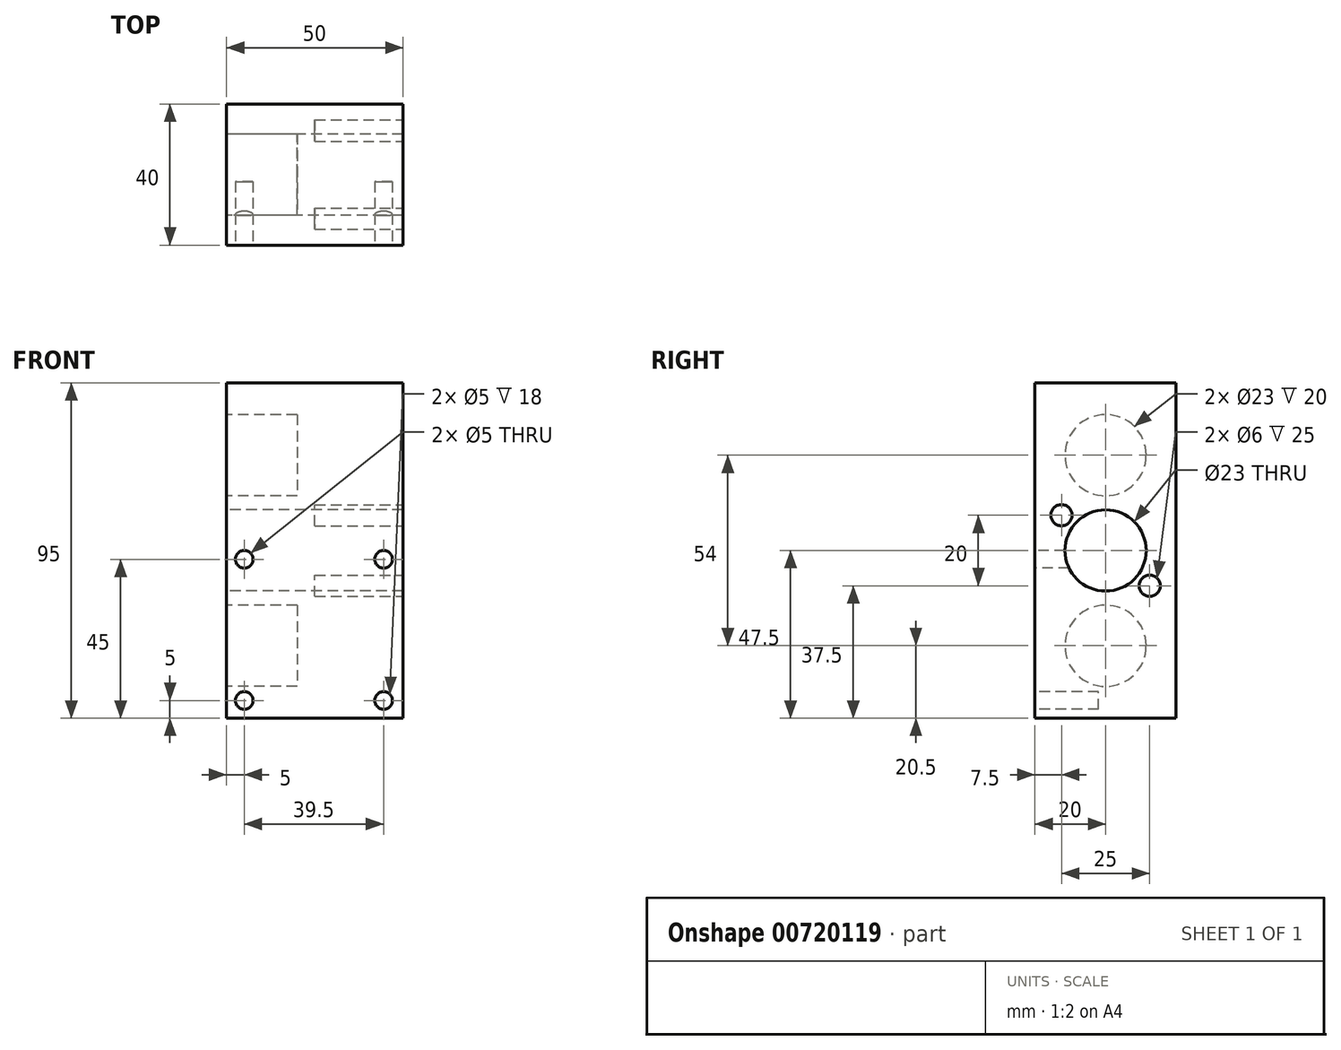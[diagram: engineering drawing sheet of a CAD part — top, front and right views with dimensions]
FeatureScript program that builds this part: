
annotation { "Feature Type Name" : "Feature", "Feature Type Description" : "" }
export const myFeature = defineFeature(function(context is Context, id is Id, definition is map)
    precondition{}
    {
        {
            var Q0;
            Q0=qCreatedBy(makeId("Front.planeOp"),FACE);
            var sketch = newSketch(context, id + "F0", { "sketchPlane" : qUnion([Q0])});
            skLineSegment(sketch, "E0.bottom", {"start": v(0, 0) * mm, "end": v(50, 0) * mm});
            skLineSegment(sketch, "E0.top", {"start": v(0, 95) * mm, "end": v(50, 95) * mm});
            skLineSegment(sketch, "E0.left", {"start": v(0, 0) * mm, "end": v(0, 95) * mm});
            skLineSegment(sketch, "E0.right", {"start": v(50, 0) * mm, "end": v(50, 95) * mm});
            skSolve(sketch);
        }
        {
            var Q0;
            Q0=makeQuery(id+"F0.imprint","IMPRINT",FACE,{"disambiguationData":[TD([[makeQuery(id+"F0.imprint","IMPRINT",EDGE,{"derivedFrom":sQuery(id+"F0.wireOp",EDGE,"E0.bottom")}),1.0]])]});
            extrude(context, id + "F1", {"entities" : qUnion([Q0]), "depth" : 40 * mm, "offsetDistance" : 25 * mm});
        }
        {
            var Q0;
            Q0=makeQuery(id+"F1.opExtrude","CAP_FACE",FACE,{"disambiguationData":[OSD([sQuery(id+"F0.wireOp",EDGE,"E0.bottom"),sQuery(id+"F0.wireOp",EDGE,"E0.top"),sQuery(id+"F0.wireOp",EDGE,"E0.left"),sQuery(id+"F0.wireOp",EDGE,"E0.right")])],"isStart":false});
            var sketch = newSketch(context, id + "F2", { "sketchPlane" : qUnion([Q0])});
            skCircle(sketch, "E1", {"center": v(5, 5) * mm, "radius": 2.5 * mm});
            skCircle(sketch, "E2", {"center": v(44.5, 5) * mm, "radius": 2.5 * mm});
            skCircle(sketch, "E3.0.1.0", {"center": v(5, 45) * mm, "radius": 2.5 * mm});
            skCircle(sketch, "E3.0.1.1", {"center": v(44.5, 45) * mm, "radius": 2.5 * mm});
            skLineSegment(sketch, "E3.direction1", {"start": v(5, 5) * mm, "end": v(30, 5) * mm, "construction": true});
            skLineSegment(sketch, "E3.direction2", {"start": v(5, 5) * mm, "end": v(5, 45) * mm, "construction": true});
            skSolve(sketch);
        }
        {
            var Q0;
            Q0 = qSketchRegion(id + "F2", true);
            extrude(context, id + "F3", {"entities" : qUnion([Q0]), "operationType" : NewBodyOperationType.REMOVE, "oppositeDirection" : true, "depth" : 18 * mm, "offsetDistance" : 25 * mm});
        }
        {
            var Q0;
            Q0=makeQuery(id+"F1.opExtrude","SWEPT_FACE",FACE,{"disambiguationData":[OSD([sQuery(id+"F0.wireOp",EDGE,"E0.left")])]});
            var sketch = newSketch(context, id + "F4", { "sketchPlane" : qUnion([Q0])});
            skCircle(sketch, "E4", {"center": v(20, 20.5) * mm, "radius": 11.5 * mm});
            skPoint(sketch, "E4.centerSnap0", {"position": v(20, 0) * mm});
            skCircle(sketch, "E5", {"center": v(20, 74.5) * mm, "radius": 11.5 * mm});
            skSolve(sketch);
        }
        {
            var Q0;
            Q0=makeQuery(id+"F4.imprint","IMPRINT",FACE,{"disambiguationData":[TD([[makeQuery(id+"F4.imprint","IMPRINT",EDGE,{"derivedFrom":sQuery(id+"F4.wireOp",EDGE,"E5")}),1.0]])]});
            var Q1;
            Q1=makeQuery(id+"F4.imprint","IMPRINT",FACE,{"disambiguationData":[TD([[makeQuery(id+"F4.imprint","IMPRINT",EDGE,{"derivedFrom":sQuery(id+"F4.wireOp",EDGE,"E4")}),1.0]])]});
            extrude(context, id + "F5", {"entities" : qUnion([Q0, Q1]), "operationType" : NewBodyOperationType.REMOVE, "oppositeDirection" : true, "depth" : 20 * mm, "offsetDistance" : 25 * mm});
        }
        {
            var Q0;
            Q0=makeQuery(id+"F1.opExtrude","SWEPT_FACE",FACE,{"disambiguationData":[OSD([sQuery(id+"F0.wireOp",EDGE,"E0.left")])]});
            var Q1;
            Q1=makeQuery(id+"F1.opExtrude","SWEPT_FACE",FACE,{"disambiguationData":[OSD([sQuery(id+"F0.wireOp",EDGE,"E0.right")])]});
            cPlane(context, id + "F6", {"entities" : qUnion([Q0, Q1]), "cplaneType" : CPlaneType.MID_PLANE, "offset" : 25 * mm, "width" : 150 * mm, "height" : 150 * mm});
        }
        {
            var Q0;
            Q0=makeQuery(id+"F1.opExtrude","SWEPT_FACE",FACE,{"disambiguationData":[OSD([sQuery(id+"F0.wireOp",EDGE,"E0.left")])]});
            var sketch = newSketch(context, id + "F7", { "sketchPlane" : qUnion([Q0])});
            skCircle(sketch, "E6", {"center": v(20, 47.5) * mm, "radius": 11.5 * mm});
            skPoint(sketch, "E6.centerSnap0", {"position": v(20, 0) * mm});
            skSolve(sketch);
        }
        {
            var Q0;
            Q0=makeQuery(id+"F7.imprint","IMPRINT",FACE,{"disambiguationData":[TD([[makeQuery(id+"F7.imprint","IMPRINT",EDGE,{"derivedFrom":sQuery(id+"F7.wireOp",EDGE,"E6")}),1.0]])]});
            extrude(context, id + "F8", {"entities" : qUnion([Q0]), "operationType" : NewBodyOperationType.REMOVE, "endBound" : BoundingType.THROUGH_ALL, "oppositeDirection" : true, "depth" : 25 * mm, "offsetDistance" : 25 * mm});
        }
        {
            var Q0;
            Q0=makeQuery(id+"F1.opExtrude","SWEPT_FACE",FACE,{"disambiguationData":[OSD([sQuery(id+"F0.wireOp",EDGE,"E0.right")])]});
            var sketch = newSketch(context, id + "F9", { "sketchPlane" : qUnion([Q0])});
            skCircle(sketch, "E7", {"center": v(-32.5, 57.5) * mm, "radius": 3 * mm});
            skCircle(sketch, "E8", {"center": v(-7.5, 37.5) * mm, "radius": 3 * mm});
            skSolve(sketch);
        }
        {
            var Q0;
            Q0=makeQuery(id+"F9.imprint","IMPRINT",FACE,{"disambiguationData":[TD([[makeQuery(id+"F9.imprint","IMPRINT",EDGE,{"derivedFrom":sQuery(id+"F9.wireOp",EDGE,"E7")}),1.0]])]});
            var Q1;
            Q1=makeQuery(id+"F9.imprint","IMPRINT",FACE,{"disambiguationData":[TD([[makeQuery(id+"F9.imprint","IMPRINT",EDGE,{"derivedFrom":sQuery(id+"F9.wireOp",EDGE,"E8")}),1.0]])]});
            extrude(context, id + "F10", {"entities" : qUnion([Q0, Q1]), "operationType" : NewBodyOperationType.REMOVE, "oppositeDirection" : true, "depth" : 25 * mm, "offsetDistance" : 25 * mm});
        }
    });
